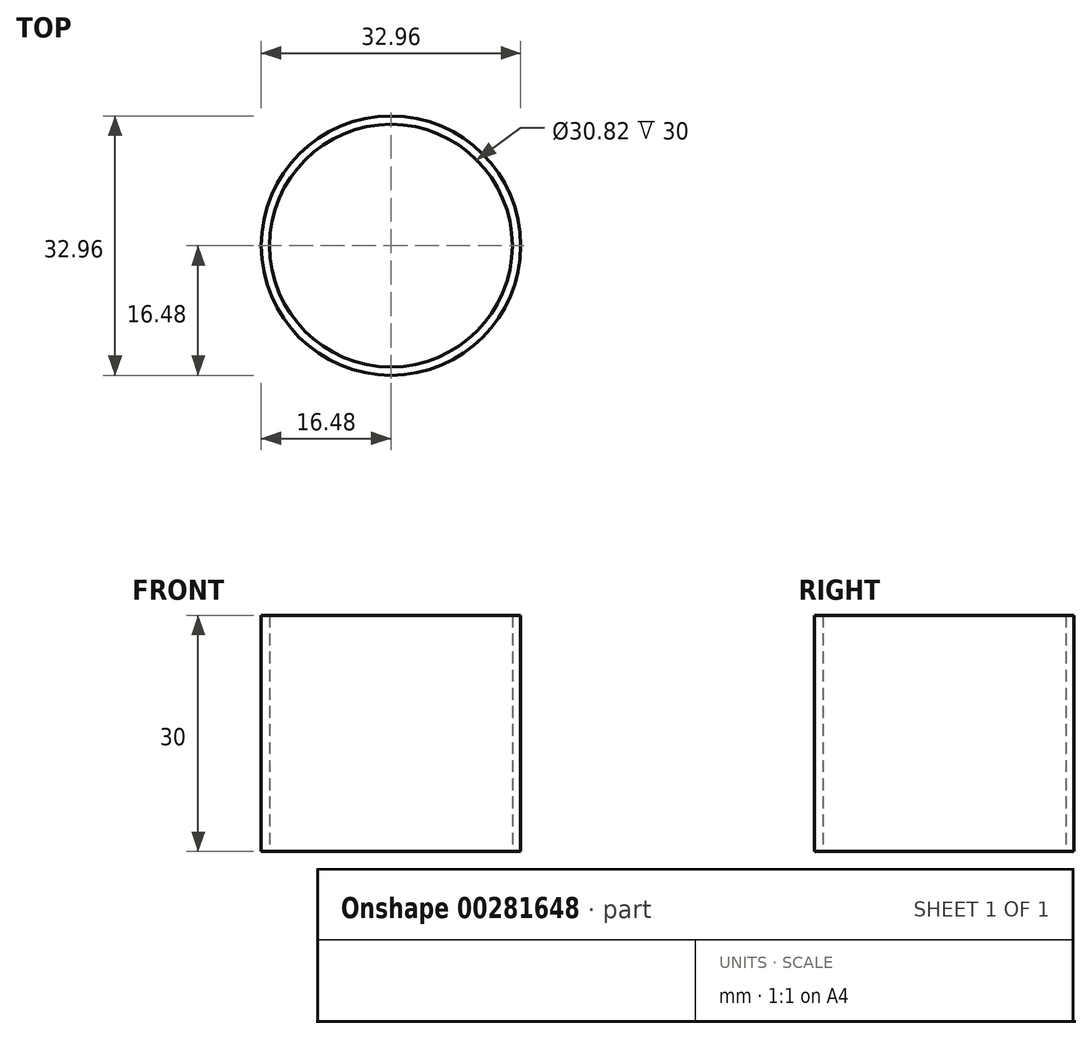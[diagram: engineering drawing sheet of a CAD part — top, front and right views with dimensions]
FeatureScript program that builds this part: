
annotation { "Feature Type Name" : "Feature", "Feature Type Description" : "" }
export const myFeature = defineFeature(function(context is Context, id is Id, definition is map)
    precondition{}
    {
        {
            var Q0;
            Q0=qCreatedBy(makeId("Top.planeOp"),FACE);
            var sketch = newSketch(context, id + "F0", { "sketchPlane" : qUnion([Q0])});
            skCircle(sketch, "E0", {"center": v(0, 0) * mm, "radius": 16.48 * mm});
            skSolve(sketch);
        }
        {
            var Q0;
            Q0=makeQuery(id+"F0.imprint","IMPRINT",FACE,{"disambiguationData":[TD([[makeQuery(id+"F0.imprint","IMPRINT",EDGE,{"derivedFrom":sQuery(id+"F0.wireOp",EDGE,"E0")}),1.0]])]});
            extrude(context, id + "F1", {"entities" : qUnion([Q0]), "depth" : 30 * mm, "offsetDistance" : 25 * mm});
        }
        {
            var Q0;
            Q0=makeQuery(id+"F1.opExtrude","CAP_FACE",FACE,{"disambiguationData":[OSD([sQuery(id+"F0.wireOp",EDGE,"E0")])],"isStart":true});
            var sketch = newSketch(context, id + "F2", { "sketchPlane" : qUnion([Q0])});
            skCircle(sketch, "E1", {"center": v(0, 0) * mm, "radius": 15.4 * mm});
            skSolve(sketch);
        }
        {
            var Q0;
            Q0=makeQuery(id+"F2.imprint","IMPRINT",FACE,{"disambiguationData":[TD([[makeQuery(id+"F2.imprint","IMPRINT",EDGE,{"derivedFrom":sQuery(id+"F2.wireOp",EDGE,"E1")}),1.0]])]});
            extrude(context, id + "F3", {"entities" : qUnion([Q0]), "operationType" : NewBodyOperationType.REMOVE, "endBound" : BoundingType.THROUGH_ALL, "oppositeDirection" : true, "depth" : 25 * mm, "offsetDistance" : 25 * mm});
        }
    });
